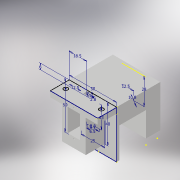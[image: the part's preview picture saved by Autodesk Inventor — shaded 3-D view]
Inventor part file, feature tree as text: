
AUTODESK INVENTOR PART (.ipt)
format: ipt  version: 2021 (Build 250183000, 183)  size: 271,360 bytes
history: native  units: in
note: dims shown in document units (in); Inventor stores cm internally (conversion verified against a paired STEP export)
features: extrude x14, sketch x13, thicken_offset x6, hole x3
ambient origin geometry x8: Origin, YZ Plane, XZ Plane, XY Plane, X Axis, Y Axis, Z Axis, Center Point
bodies: Solid1 (feature_tree)
feature tree (36):
  sketch  "Sketch1"  dims[d4=1.9685in d5=1.9685in]
  sketch  "Sketch2"  dims[d6=0.5118in d7=0.9055in]
  extrude  "Extrusion1"  Depth=1.9685in
  extrude  "Extrusion2"  Depth=0.9055in
  extrude  "Extrusion3"  Depth=0.2362in
  extrude  "Extrusion4"  Depth=0.0591in
  extrude  "Extrusion5"  Depth=0.0591in
  sketch  "Sketch3"  dims[d8=0.7283in d9=0.2362in]
  extrude  "Extrusion6"  Depth=0.9843in
  extrude  "Extrusion7"  Depth=0.4921in
  hole  "Hole1"  [1 undecoded]
  extrude  "Extrusion8"  Depth=0.1181in TaperAngle=0.0deg
  extrude  "Extrusion9"  Depth=1.5748in TaperAngle=0.0deg
  extrude  "Extrusion10"  Depth=0.9843in
  extrude  "Extrusion11"  Depth=1.1811in
  extrude  "Extrusion12"  Depth=0.4921in
  thicken_offset  "Thicken1"
  thicken_offset  "Thicken2"
  thicken_offset  "Thicken3"
  thicken_offset  "Thicken4"
  sketch  "Sketch8"  dims[d19=0.7874in d20=0.0in d21=0.1181in d22=0.0in]
  extrude  "Extrusion13"  Depth=0.3937in
  thicken_offset  "Thicken5"
  thicken_offset  "Thicken6"
  extrude  "Extrusion14"  Depth=0.1969in
  sketch  "Sketch10"  dims[d27=0.1181in d28=0.0in d29=1.5748in d30=0.0in]
  hole  "Hole2"  [1 undecoded]
  hole  "Hole3"  [1 undecoded]
  sketch  "Sketch13"  dims[d36=1.1024in d37=0.4921in d38=0.4252in d39=0.2362in d40=0.1575in d41=0.0787in d42=90.0deg d43=0.315in d44=0.8108in d47=0.3937in d48=0.1969in d49=0.2953in d50=0.3937in d51=0.0in d52=0.0787in d53=0.0in d54=0.1181in d55=0.0in d56=0.1181in d57=0.0in d58=0.1575in d59=0.0in d60=0.4921in d61=0.4921in d62=0.4921in d63=0.4921in d64=0.0197in d65=0.0197in d66=0.0197in d67=0.0197in d68=0.7795in d69=0.2677in d70=0.0in d71=0.1566in d72=0.1566in d73=0.1181in d74=0.1181in d75=0.2362in d76=0.0in d77=0.1693in d78=0.2362in d79=0.1575in d80=0.0787in d81=90.0deg d82=0.315in d83=0.8108in d84=0.1693in d85=0.2362in d86=0.1575in d87=0.0787in d88=90.0deg d89=0.315in d90=0.8108in d45=0.0295in d46=0.8108in]
  sketch  "Sketch4"  dims[d10=0.0591in d11=0.2559in]
  sketch  "Sketch5"  dims[d12=0.1102in d13=0.0591in d14=0.2559in]
  sketch  "Sketch6"  dims[d15=0.1102in d16=0.9843in]
  sketch  "Sketch7"  dims[d17=1.5748in d18=0.4921in]
  sketch  "Sketch9"  dims[d23=0.1181in d24=0.0in d25=0.1181in d26=0.0in]
  sketch  "Sketch11"  dims[d31=0.9843in d32=0.4724in]
  sketch  "Sketch12"  dims[d33=1.1811in d34=0.0in d35=0.4252in]
note: 3 required parameter values undecoded (feature->parameter linkage not recoverable at this tier; creation-order binding heuristic only, values carry confidence <= 0.55)
